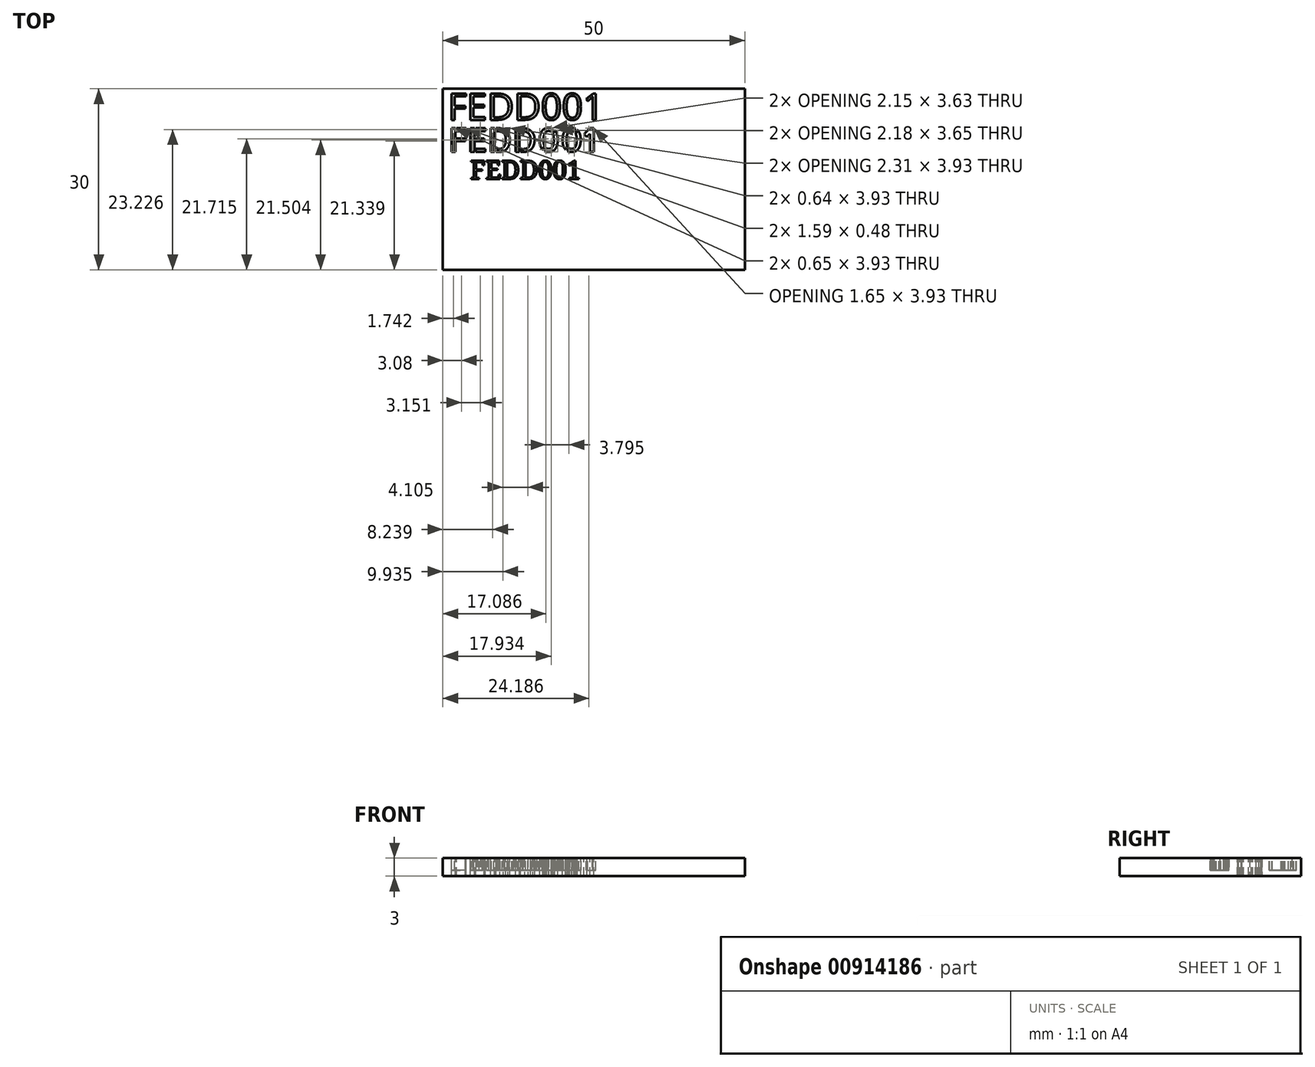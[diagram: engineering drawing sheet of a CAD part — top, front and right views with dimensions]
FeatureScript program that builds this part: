
annotation { "Feature Type Name" : "Feature", "Feature Type Description" : "" }
export const myFeature = defineFeature(function(context is Context, id is Id, definition is map)
    precondition{}
    {
        {
            var Q0;
            Q0=qCreatedBy(makeId("Top.planeOp"),FACE);
            var sketch = newSketch(context, id + "F0", { "sketchPlane" : qUnion([Q0])});
            skLineSegment(sketch, "E0.bottom", {"start": v(-20.75, 10.46) * mm, "end": v(29.25, 10.46) * mm});
            skLineSegment(sketch, "E0.top", {"start": v(-20.75, -19.54) * mm, "end": v(29.25, -19.54) * mm});
            skLineSegment(sketch, "E0.left", {"start": v(-20.75, 10.46) * mm, "end": v(-20.75, -19.54) * mm});
            skLineSegment(sketch, "E0.right", {"start": v(29.25, 10.46) * mm, "end": v(29.25, -19.54) * mm});
            skSolve(sketch);
        }
        {
            var Q0;
            Q0=makeQuery(id+"F0.imprint","IMPRINT",FACE,{"disambiguationData":[TD([[makeQuery(id+"F0.imprint","IMPRINT",EDGE,{"derivedFrom":sQuery(id+"F0.wireOp",EDGE,"E0.bottom")}),-1.0]])]});
            extrude(context, id + "F1", {"entities" : qUnion([Q0]), "depth" : 3 * mm, "offsetDistance" : 25 * mm});
        }
        {
            var Q0;
            Q0=makeQuery(id+"F1.opExtrude","CAP_FACE",FACE,{"disambiguationData":[OSD([sQuery(id+"F0.wireOp",EDGE,"E0.bottom"),sQuery(id+"F0.wireOp",EDGE,"E0.top"),sQuery(id+"F0.wireOp",EDGE,"E0.left"),sQuery(id+"F0.wireOp",EDGE,"E0.right")])],"isStart":false});
            var sketch = newSketch(context, id + "F2", { "sketchPlane" : qUnion([Q0])});
            skText(sketch, "E1", { "text": "FEDD001", "fontName": "OpenSans-Regular.ttf"});
            const initialGuessF2  = {"E1": [-0.01993, 0.0053, 1, 0, 0.00438]};
            skSetInitialGuess(sketch, initialGuessF2);
            skSolve(sketch);
        }
        {
            var Q0;
            Q0=makeQuery(id+"F2.imprint","IMPRINT",FACE,{"disambiguationData":[TD([[makeQuery(id+"F2.imprint","IMPRINT",EDGE,{"derivedFrom":sQuery(id+"F2.wireOp",EDGE,"E1.sketch_text.stroke-0")}),-1.0]])]});
            var Q1;
            Q1=makeQuery(id+"F2.imprint","IMPRINT",FACE,{"disambiguationData":[TD([[makeQuery(id+"F2.imprint","IMPRINT",EDGE,{"derivedFrom":sQuery(id+"F2.wireOp",EDGE,"E1.sketch_text.stroke-10")}),-1.0]])]});
            var Q2;
            Q2=makeQuery(id+"F2.imprint","IMPRINT",FACE,{"disambiguationData":[TD([[makeQuery(id+"F2.imprint","IMPRINT",EDGE,{"derivedFrom":sQuery(id+"F2.wireOp",EDGE,"E1.sketch_text.stroke-22")}),-1.0]])]});
            var Q3;
            Q3=makeQuery(id+"F2.imprint","IMPRINT",FACE,{"disambiguationData":[TD([[makeQuery(id+"F2.imprint","IMPRINT",EDGE,{"derivedFrom":sQuery(id+"F2.wireOp",EDGE,"E1.sketch_text.stroke-36")}),-1.0]])]});
            var Q4;
            Q4=makeQuery(id+"F2.imprint","IMPRINT",FACE,{"disambiguationData":[TD([[makeQuery(id+"F2.imprint","IMPRINT",EDGE,{"derivedFrom":sQuery(id+"F2.wireOp",EDGE,"E1.sketch_text.stroke-50")}),-1.0]])]});
            var Q5;
            Q5=makeQuery(id+"F2.imprint","IMPRINT",FACE,{"disambiguationData":[TD([[makeQuery(id+"F2.imprint","IMPRINT",EDGE,{"derivedFrom":sQuery(id+"F2.wireOp",EDGE,"E1.sketch_text.stroke-66")}),-1.0]])]});
            var Q6;
            Q6=makeQuery(id+"F2.imprint","IMPRINT",FACE,{"disambiguationData":[TD([[makeQuery(id+"F2.imprint","IMPRINT",EDGE,{"derivedFrom":sQuery(id+"F2.wireOp",EDGE,"E1.sketch_text.stroke-82")}),-1.0]])]});
            extrude(context, id + "F3", {"entities" : qUnion([Q0, Q1, Q2, Q3, Q4, Q5, Q6]), "operationType" : NewBodyOperationType.REMOVE, "oppositeDirection" : true, "depth" : 2 * mm, "offsetDistance" : 25 * mm});
        }
        {
            var Q0;
            {var subQ0=sQuery(id+"F0.wireOp",EDGE,"E0.left");var subQ1=sQuery(id+"F0.wireOp",EDGE,"E0.bottom");var subQ2=sQuery(id+"F0.wireOp",EDGE,"E0.right");var subQ3=sQuery(id+"F0.wireOp",EDGE,"E0.top");Q0=makeQuery(id+"F3.boolean.opBoolean","SPLIT",FACE,{"disambiguationData":[TD([makeQuery(id+"F1.opExtrude","SWEPT_FACE",FACE,{"disambiguationData":[OSD([subQ1])]})])],"derivedFrom":makeQuery(id+"F1.opExtrude","CAP_FACE",FACE,{"disambiguationData":[OSD([subQ1,subQ3,subQ0,subQ2])],"isStart":false})});}
            var sketch = newSketch(context, id + "F4", { "sketchPlane" : qUnion([Q0])});
            skText(sketch, "E2", { "text": "FEDD001", "fontName": "AllertaStencil-Regular.ttf"});
            const initialGuessF4  = {"E2": [-0.01984, 0, 1, 0, 0.00393]};
            skSetInitialGuess(sketch, initialGuessF4);
            skSolve(sketch);
        }
        {
            var Q0;
            Q0=makeQuery(id+"F4.imprint","IMPRINT",FACE,{"disambiguationData":[TD([[makeQuery(id+"F4.imprint","IMPRINT",EDGE,{"derivedFrom":sQuery(id+"F4.wireOp",EDGE,"E2.sketch_text.stroke-0")}),-1.0]])]});
            var Q1;
            Q1=makeQuery(id+"F4.imprint","IMPRINT",FACE,{"disambiguationData":[TD([[makeQuery(id+"F4.imprint","IMPRINT",EDGE,{"derivedFrom":sQuery(id+"F4.wireOp",EDGE,"E2.sketch_text.stroke-4")}),-1.0]])]});
            var Q2;
            Q2=makeQuery(id+"F4.imprint","IMPRINT",FACE,{"disambiguationData":[TD([[makeQuery(id+"F4.imprint","IMPRINT",EDGE,{"derivedFrom":sQuery(id+"F4.wireOp",EDGE,"E2.sketch_text.stroke-8")}),-1.0]])]});
            var Q3;
            Q3=makeQuery(id+"F4.imprint","IMPRINT",FACE,{"disambiguationData":[TD([[makeQuery(id+"F4.imprint","IMPRINT",EDGE,{"derivedFrom":sQuery(id+"F4.wireOp",EDGE,"E2.sketch_text.stroke-12")}),-1.0]])]});
            var Q4;
            Q4=makeQuery(id+"F4.imprint","IMPRINT",FACE,{"disambiguationData":[TD([[makeQuery(id+"F4.imprint","IMPRINT",EDGE,{"derivedFrom":sQuery(id+"F4.wireOp",EDGE,"E2.sketch_text.stroke-16")}),-1.0]])]});
            var Q5;
            Q5=makeQuery(id+"F4.imprint","IMPRINT",FACE,{"disambiguationData":[TD([[makeQuery(id+"F4.imprint","IMPRINT",EDGE,{"derivedFrom":sQuery(id+"F4.wireOp",EDGE,"E2.sketch_text.stroke-24")}),-1.0]])]});
            var Q6;
            Q6=makeQuery(id+"F4.imprint","IMPRINT",FACE,{"disambiguationData":[TD([[makeQuery(id+"F4.imprint","IMPRINT",EDGE,{"derivedFrom":sQuery(id+"F4.wireOp",EDGE,"E2.sketch_text.stroke-20")}),-1.0]])]});
            var Q7;
            Q7=makeQuery(id+"F4.imprint","IMPRINT",FACE,{"disambiguationData":[TD([[makeQuery(id+"F4.imprint","IMPRINT",EDGE,{"derivedFrom":sQuery(id+"F4.wireOp",EDGE,"E2.sketch_text.stroke-28")}),-1.0]])]});
            var Q8;
            Q8=makeQuery(id+"F4.imprint","IMPRINT",FACE,{"disambiguationData":[TD([[makeQuery(id+"F4.imprint","IMPRINT",EDGE,{"derivedFrom":sQuery(id+"F4.wireOp",EDGE,"E2.sketch_text.stroke-32")}),-1.0]])]});
            var Q9;
            Q9=makeQuery(id+"F4.imprint","IMPRINT",FACE,{"disambiguationData":[TD([[makeQuery(id+"F4.imprint","IMPRINT",EDGE,{"derivedFrom":sQuery(id+"F4.wireOp",EDGE,"E2.sketch_text.stroke-54")}),-1.0]])]});
            var Q10;
            Q10=makeQuery(id+"F4.imprint","IMPRINT",FACE,{"disambiguationData":[TD([[makeQuery(id+"F4.imprint","IMPRINT",EDGE,{"derivedFrom":sQuery(id+"F4.wireOp",EDGE,"E2.sketch_text.stroke-58")}),-1.0]])]});
            var Q11;
            Q11=makeQuery(id+"F4.imprint","IMPRINT",FACE,{"disambiguationData":[TD([[makeQuery(id+"F4.imprint","IMPRINT",EDGE,{"derivedFrom":sQuery(id+"F4.wireOp",EDGE,"E2.sketch_text.stroke-80")}),-1.0]])]});
            var Q12;
            Q12=makeQuery(id+"F4.imprint","IMPRINT",FACE,{"disambiguationData":[TD([[makeQuery(id+"F4.imprint","IMPRINT",EDGE,{"derivedFrom":sQuery(id+"F4.wireOp",EDGE,"E2.sketch_text.stroke-96")}),-1.0]])]});
            var Q13;
            Q13=makeQuery(id+"F4.imprint","IMPRINT",FACE,{"disambiguationData":[TD([[makeQuery(id+"F4.imprint","IMPRINT",EDGE,{"derivedFrom":sQuery(id+"F4.wireOp",EDGE,"E2.sketch_text.stroke-113")}),-1.0]])]});
            var Q14;
            Q14=makeQuery(id+"F4.imprint","IMPRINT",FACE,{"disambiguationData":[TD([[makeQuery(id+"F4.imprint","IMPRINT",EDGE,{"derivedFrom":sQuery(id+"F4.wireOp",EDGE,"E2.sketch_text.stroke-129")}),-1.0]])]});
            var Q15;
            Q15=makeQuery(id+"F4.imprint","IMPRINT",FACE,{"disambiguationData":[TD([[makeQuery(id+"F4.imprint","IMPRINT",EDGE,{"derivedFrom":sQuery(id+"F4.wireOp",EDGE,"E2.sketch_text.stroke-146")}),-1.0]])]});
            extrude(context, id + "F5", {"entities" : qUnion([Q0, Q1, Q2, Q3, Q4, Q5, Q6, Q7, Q8, Q9, Q10, Q11, Q12, Q13, Q14, Q15]), "operationType" : NewBodyOperationType.REMOVE, "oppositeDirection" : true, "depth" : 3 * mm, "offsetDistance" : 25 * mm});
        }
        {
            var Q0;
            {var subQ0=sQuery(id+"F0.wireOp",EDGE,"E0.left");var subQ1=sQuery(id+"F0.wireOp",EDGE,"E0.bottom");var subQ2=sQuery(id+"F0.wireOp",EDGE,"E0.right");var subQ3=sQuery(id+"F0.wireOp",EDGE,"E0.top");Q0=makeQuery(id+"F3.boolean.opBoolean","SPLIT",FACE,{"disambiguationData":[TD([makeQuery(id+"F1.opExtrude","SWEPT_FACE",FACE,{"disambiguationData":[OSD([subQ1])]})])],"derivedFrom":makeQuery(id+"F1.opExtrude","CAP_FACE",FACE,{"disambiguationData":[OSD([subQ1,subQ3,subQ0,subQ2])],"isStart":false})});}
            var sketch = newSketch(context, id + "F6", { "sketchPlane" : qUnion([Q0])});
            skText(sketch, "E3", { "text": "FEDD001", "fontName": "NotoSerif-Regular.ttf"});
            const initialGuessF6  = {"E3": [-0.01622, -0.00449, 1, 0, 0.00304]};
            skSetInitialGuess(sketch, initialGuessF6);
            skSolve(sketch);
        }
        {
            var Q0;
            Q0=makeQuery(id+"F6.imprint","IMPRINT",FACE,{"disambiguationData":[TD([[makeQuery(id+"F6.imprint","IMPRINT",EDGE,{"derivedFrom":sQuery(id+"F6.wireOp",EDGE,"E3.sketch_text.stroke-0")}),-1.0]])]});
            var Q1;
            Q1=makeQuery(id+"F6.imprint","IMPRINT",FACE,{"disambiguationData":[TD([[makeQuery(id+"F6.imprint","IMPRINT",EDGE,{"derivedFrom":sQuery(id+"F6.wireOp",EDGE,"E3.sketch_text.stroke-34")}),-1.0]])]});
            var Q2;
            Q2=makeQuery(id+"F6.imprint","IMPRINT",FACE,{"disambiguationData":[TD([[makeQuery(id+"F6.imprint","IMPRINT",EDGE,{"derivedFrom":sQuery(id+"F6.wireOp",EDGE,"E3.sketch_text.stroke-70")}),-1.0]])]});
            var Q3;
            Q3=makeQuery(id+"F6.imprint","IMPRINT",FACE,{"disambiguationData":[TD([[makeQuery(id+"F6.imprint","IMPRINT",EDGE,{"derivedFrom":sQuery(id+"F6.wireOp",EDGE,"E3.sketch_text.stroke-102")}),-1.0]])]});
            var Q4;
            Q4=makeQuery(id+"F6.imprint","IMPRINT",FACE,{"disambiguationData":[TD([[makeQuery(id+"F6.imprint","IMPRINT",EDGE,{"derivedFrom":sQuery(id+"F6.wireOp",EDGE,"E3.sketch_text.stroke-134")}),-1.0]])]});
            var Q5;
            Q5=makeQuery(id+"F6.imprint","IMPRINT",FACE,{"disambiguationData":[TD([[makeQuery(id+"F6.imprint","IMPRINT",EDGE,{"derivedFrom":sQuery(id+"F6.wireOp",EDGE,"E3.sketch_text.stroke-166")}),-1.0]])]});
            var Q6;
            Q6=makeQuery(id+"F6.imprint","IMPRINT",FACE,{"disambiguationData":[TD([[makeQuery(id+"F6.imprint","IMPRINT",EDGE,{"derivedFrom":sQuery(id+"F6.wireOp",EDGE,"E3.sketch_text.stroke-198")}),-1.0]])]});
            extrude(context, id + "F7", {"entities" : qUnion([Q0, Q1, Q2, Q3, Q4, Q5, Q6]), "operationType" : NewBodyOperationType.REMOVE, "oppositeDirection" : true, "depth" : 2 * mm, "offsetDistance" : 25 * mm});
        }
    });
